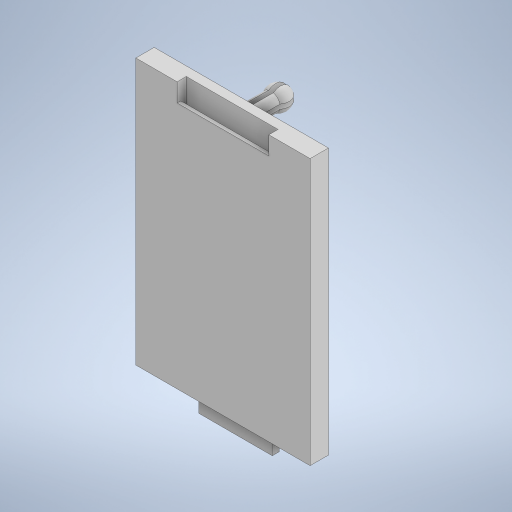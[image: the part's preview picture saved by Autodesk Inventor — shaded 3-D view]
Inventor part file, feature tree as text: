
AUTODESK INVENTOR PART (.ipt)
format: ipt  version: 2024.2 (Build 282272000, 272)  size: 315,392 bytes
history: native  units: in
note: dims shown in document units (in); Inventor stores cm internally (conversion verified against a paired STEP export)
features: extrude x7, sketch x6, chamfer x1, other x1
ambient origin geometry x8: Origin, YZ Plane, XZ Plane, XY Plane, X Axis, Y Axis, Z Axis, Center Point
bodies: Solide1 (feature_tree)
feature tree (15):
  sketch  "Esquisse1"
  extrude  "Extrusion1"  Depth=0.748in
  extrude  "Extrusion2"  Depth=1.1417in
  chamfer  "Chanfrein1"  Distance=0.0787in
  extrude  "Extrusion3"  Depth=0.0787in
  sketch  "Esquisse3"
  other  "Révolution1"
  extrude  "Extrusion6"  Depth=0.0787in TaperAngle=0.0deg
  extrude  "Extrusion7"  Depth=0.315in
  extrude  "Extrusion8"  Depth=0.1969in
  extrude  "Extrusion9"  Depth=0.0984in
  sketch  "Esquisse2"
  sketch  "Esquisse4"
  sketch  "Esquisse5"
  sketch  "Esquisse6"
